# Revit family: Tantum Triplex
name_source: partatom
category: HLS-Bauteile
units: mm (PartAtom-declared; Revit-internal decimal feet)

## family parameters
Arbeitsebenenbasiert = Nein
Beim Laden mit Abzugskörper schneiden = Nein
Bemaßung runder Anschluss = Durchmesser verwenden
Beschriftungsausrichtung beibehalten = Nein
Gemeinsam genutzt = Nein
Immer vertikal = Ja
Klassifizierung = Keine
Raumberechnungspunkt = Nein
Teiletyp = Normal

## types (5) — shared parameters
Datenblatt = https://www.burkhalter-h2o.ch
Homepage = https://www.burkhalter-h2o.ch
LUT = LUT_Tantum_Triplex
zero-valued in all types: Vorgabe-Ansicht

## per-type parameters (varying)
| type | A1 | A2 | A3 | A3.1 | B | D | DS_Oben | DS_Unten | H | H1 | H2 | Harzinhalt_pro_Harzdruckbehälter | Höhe_Behälter | R | T | T1 | X |
| Tantum Triplex - 400L | 80 mm  [stored 0.262467 ft] | 50 mm  [stored 0.164042 ft] | 32 mm  [stored 0.104987 ft] | 16 mm  [stored 0.0524934 ft] | 2810 mm | 770 mm  [stored 2.52625 ft] | 720 mm  [stored 2.3622 ft] | 820 mm  [stored 2.69029 ft] | 2280 mm | 900 mm  [stored 2.95276 ft] | 700 mm  [stored 2.29659 ft] | 400L | 1880 mm | 385 mm  [stored 1.26312 ft] | 1550 mm | 520 mm  [stored 1.70604 ft] | 900 mm  [stored 2.95276 ft] |
| Tantum Triplex - 600L | 100 mm  [stored 0.328084 ft] | 65 mm  [stored 0.213255 ft] | 32 mm  [stored 0.104987 ft] | 16 mm  [stored 0.0524934 ft] | 3360 mm | 927 mm  [stored 3.04134 ft] | 877 mm  [stored 2.8773 ft] | 977 mm  [stored 3.20538 ft] | 2690 mm | 1000 mm  [stored 3.28084 ft] | 800 mm  [stored 2.62467 ft] | 600L | 2290 mm | 464 mm | 1700 mm | 590 mm  [stored 1.9357 ft] | 1100 mm  [stored 3.60892 ft] |
| Tantum Triplex - 900L | 125 mm  [stored 0.410105 ft] | 65 mm  [stored 0.213255 ft] | 40 mm  [stored 0.131234 ft] | 20 mm  [stored 0.0656168 ft] | 3640 mm | 1074 mm  [stored 3.52362 ft] | 1024 mm  [stored 3.35958 ft] | 1124 mm  [stored 3.68766 ft] | 2780 mm | 1000 mm  [stored 3.28084 ft] | 800 mm  [stored 2.62467 ft] | 900L | 2380 mm | 537 mm  [stored 1.76181 ft] | 1850 mm | 670 mm  [stored 2.19816 ft] | 1200 mm  [stored 3.93701 ft] |
| Tantum Triplex - 1100L | 125 mm  [stored 0.410105 ft] | 80 mm  [stored 0.262467 ft] | 50 mm  [stored 0.164042 ft] | 25 mm  [stored 0.082021 ft] | 4190 mm | 1226 mm  [stored 4.02231 ft] | 1176 mm  [stored 3.85827 ft] | 1276 mm  [stored 4.18635 ft] | 2840 mm | 1000 mm  [stored 3.28084 ft] | 800 mm  [stored 2.62467 ft] | 1100L | 2440 mm | 613 mm  [stored 2.01115 ft] | 2000 mm | 740 mm  [stored 2.42782 ft] | 1400 mm |
| Tantum Triplex - 1650L | 150 mm  [stored 0.492126 ft] | 80 mm  [stored 0.262467 ft] | 50 mm  [stored 0.164042 ft] | 25 mm  [stored 0.082021 ft] | 4890 mm | 1429 mm | 1379 mm | 1479 mm | 3460 mm | 1000 mm  [stored 3.28084 ft] | 800 mm  [stored 2.62467 ft] | 1650L | 3060 mm | 715 mm | 2200 mm | 840 mm  [stored 2.75591 ft] | 1700 mm |

note: [stored X ft] marks values corroborated as IEEE doubles in the binary element streams (Revit-internal decimal feet)
